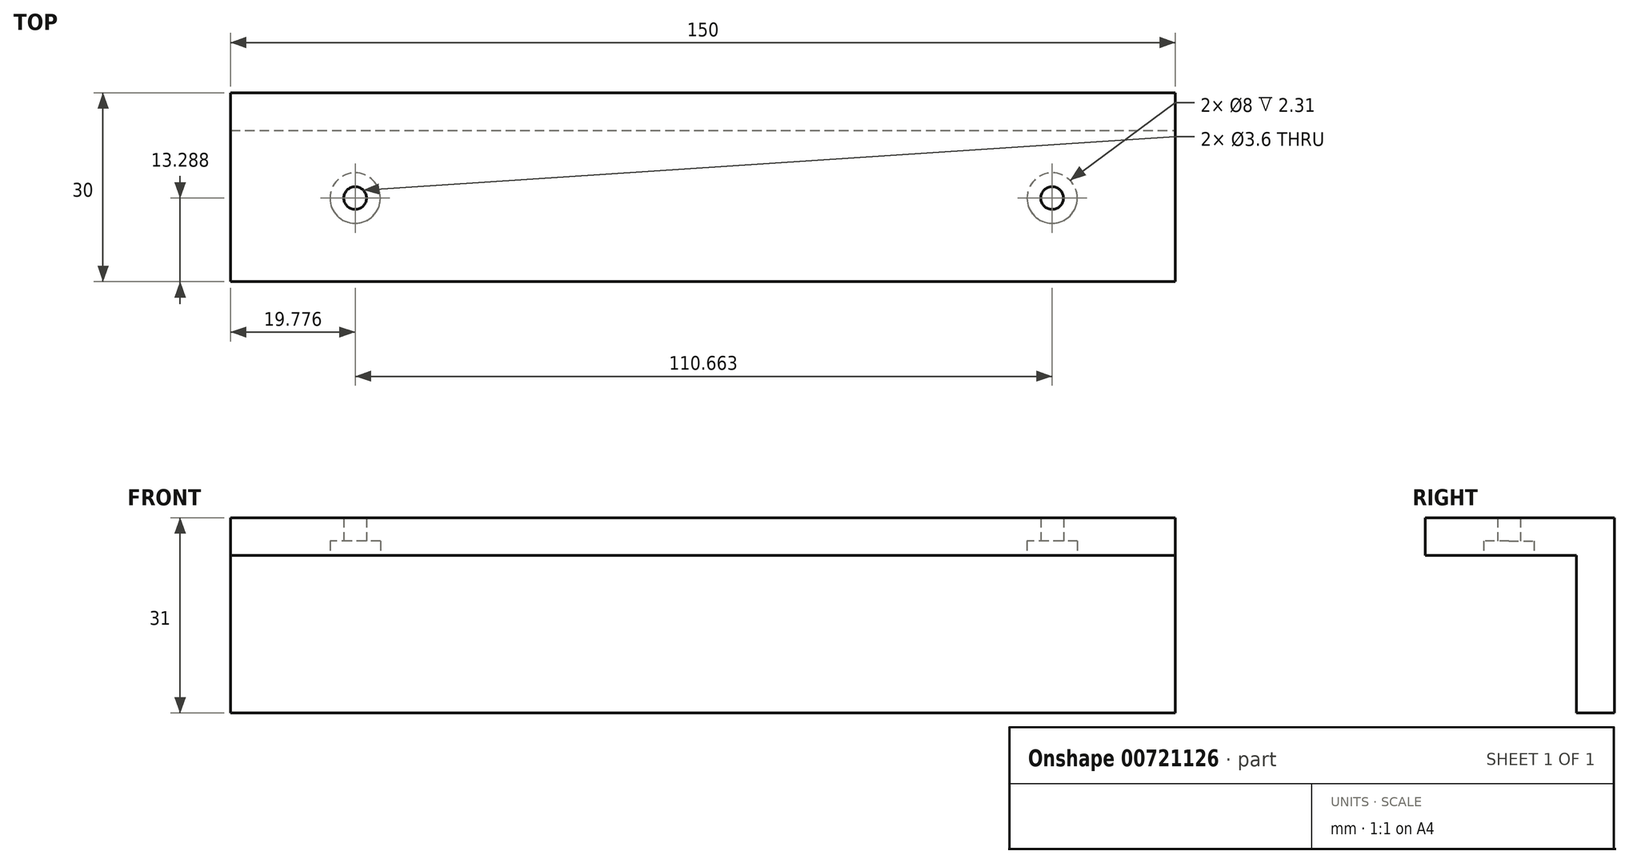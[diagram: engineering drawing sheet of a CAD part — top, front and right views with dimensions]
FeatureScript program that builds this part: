
annotation { "Feature Type Name" : "Feature", "Feature Type Description" : "" }
export const myFeature = defineFeature(function(context is Context, id is Id, definition is map)
    precondition{}
    {
        {
            var Q0;
            Q0=qCreatedBy(makeId("Front.planeOp"),FACE);
            var sketch = newSketch(context, id + "F0", { "sketchPlane" : qUnion([Q0])});
            skLineSegment(sketch, "E0", {"start": v(-38.58, 25) * mm, "end": v(-38.58, 0) * mm});
            skLineSegment(sketch, "E1", {"start": v(-38.58, 0) * mm, "end": v(111.42, 0) * mm});
            skLineSegment(sketch, "E2", {"start": v(111.42, 0) * mm, "end": v(111.42, 25) * mm});
            skLineSegment(sketch, "E3", {"start": v(111.42, 25) * mm, "end": v(-38.58, 25) * mm});
            skLineSegment(sketch, "E4", {"start": v(111.42, 25) * mm, "end": v(111.42, 31) * mm});
            skLineSegment(sketch, "E5", {"start": v(111.42, 31) * mm, "end": v(-38.58, 31) * mm});
            skLineSegment(sketch, "E6", {"start": v(-38.58, 31) * mm, "end": v(-38.58, 25) * mm});
            skSolve(sketch);
        }
        {
            var Q0;
            Q0 = qSketchRegion(id + "F0", true);
            extrude(context, id + "F1", {"entities" : qUnion([Q0]), "depth" : 6 * mm, "offsetDistance" : 25 * mm});
        }
        {
            var Q0;
            Q0=makeQuery(id+"F0.imprint","IMPRINT",FACE,{"disambiguationData":[TD([[makeQuery(id+"F0.imprint","IMPRINT",EDGE,{"derivedFrom":sQuery(id+"F0.wireOp",EDGE,"E3")}),-1.0]])]});
            extrude(context, id + "F2", {"entities" : qUnion([Q0]), "operationType" : NewBodyOperationType.ADD, "depth" : 30 * mm, "offsetDistance" : 25 * mm});
        }
        {
            var Q0;
            Q0=qCreatedBy(makeId("Top.planeOp"),FACE);
            var sketch = newSketch(context, id + "F3", { "sketchPlane" : qUnion([Q0])});
            skLineSegment(sketch, "E7", {"start": v(-22.06, -0.64) * mm, "end": v(127.48, -0.64) * mm});
            skCircle(sketch, "E8", {"center": v(-18.8, -16.71) * mm, "radius": 1.8 * mm});
            skCircle(sketch, "E9", {"center": v(91.86, -16.71) * mm, "radius": 1.8 * mm});
            skLineSegment(sketch, "E10", {"start": v(-18.8, -16.71) * mm, "end": v(-38.47, -16.71) * mm, "construction": true});
            skLineSegment(sketch, "E11", {"start": v(91.86, -16.71) * mm, "end": v(111.53, -16.71) * mm, "construction": true});
            skLineSegment(sketch, "E12", {"start": v(-38.47, -16.71) * mm, "end": v(-38.47, -30.2) * mm, "construction": true});
            skLineSegment(sketch, "E13", {"start": v(-38.47, -30.2) * mm, "end": v(111.53, -30.2) * mm, "construction": true});
            skLineSegment(sketch, "E14", {"start": v(111.53, -30.2) * mm, "end": v(111.53, -16.71) * mm, "construction": true});
            skLineSegment(sketch, "E15", {"start": v(-18.8, -16.71) * mm, "end": v(91.86, -16.71) * mm, "construction": true});
            skCircle(sketch, "E16", {"center": v(-18.8, -16.71) * mm, "radius": 4 * mm});
            skCircle(sketch, "E17", {"center": v(91.86, -16.71) * mm, "radius": 4 * mm});
            skSolve(sketch);
        }
        {
            var Q0;
            Q0=makeQuery(id+"F3.imprint","IMPRINT",FACE,{"disambiguationData":[TD([[makeQuery(id+"F3.imprint","IMPRINT",EDGE,{"derivedFrom":sQuery(id+"F3.wireOp",EDGE,"E9")}),-1.0]])]});
            var Q1;
            Q1=makeQuery(id+"F3.imprint","IMPRINT",FACE,{"disambiguationData":[TD([[makeQuery(id+"F3.imprint","IMPRINT",EDGE,{"derivedFrom":sQuery(id+"F3.wireOp",EDGE,"E8")}),-1.0]])]});
            extrude(context, id + "F4", {"entities" : qUnion([Q0, Q1]), "operationType" : NewBodyOperationType.REMOVE, "oppositeDirection" : true, "depth" : -27.3 * mm, "offsetDistance" : 25 * mm});
        }
        {
            var Q0;
            Q0=makeQuery(id+"F4.boolean.opBoolean","SPLIT",FACE,{"disambiguationData":[TD([makeQuery(id+"F4.opExtrude","SWEPT_FACE",FACE,{"disambiguationData":[OSD([sQuery(id+"F3.wireOp",EDGE,"E8")])]})])],"derivedFrom":makeQuery(id+"F2.opExtrude","SWEPT_FACE",FACE,{"disambiguationData":[OSD([sQuery(id+"F0.wireOp",EDGE,"E3")])]})});
            var Q1;
            Q1=makeQuery(id+"F4.boolean.opBoolean","SPLIT",FACE,{"disambiguationData":[TD([makeQuery(id+"F4.opExtrude","SWEPT_FACE",FACE,{"disambiguationData":[OSD([sQuery(id+"F3.wireOp",EDGE,"E9")])]})])],"derivedFrom":makeQuery(id+"F2.opExtrude","SWEPT_FACE",FACE,{"disambiguationData":[OSD([sQuery(id+"F0.wireOp",EDGE,"E3")])]})});
            extrude(context, id + "F5", {"entities" : qUnion([Q0, Q1]), "operationType" : NewBodyOperationType.REMOVE, "oppositeDirection" : true, "depth" : 25 * mm, "offsetDistance" : 25 * mm});
        }
    });
